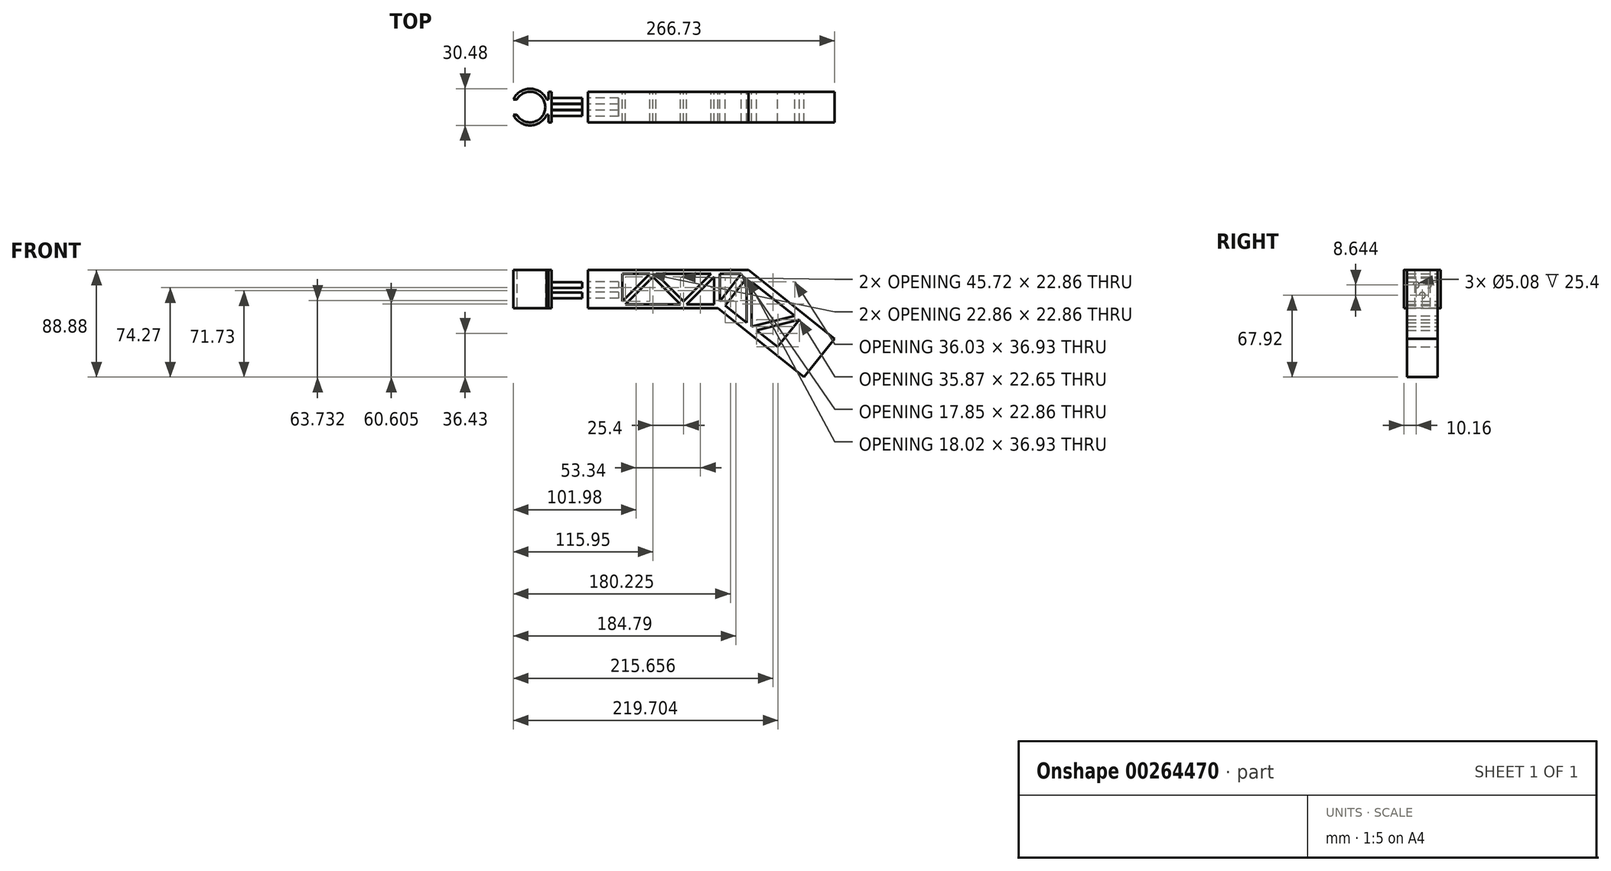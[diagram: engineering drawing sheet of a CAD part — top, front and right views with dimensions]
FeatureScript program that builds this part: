
annotation { "Feature Type Name" : "Feature", "Feature Type Description" : "" }
export const myFeature = defineFeature(function(context is Context, id is Id, definition is map)
    precondition{}
    {
        {
            var Q0;
            Q0=qCreatedBy(makeId("Front.planeOp"),FACE);
            var sketch = newSketch(context, id + "F0", { "sketchPlane" : qUnion([Q0])});
            skLineSegment(sketch, "E0.top", {"start": v(101.6, -25.4) * mm, "end": v(55.88, -25.4) * mm});
            skLineSegment(sketch, "E0.left", {"start": v(101.6, 20.32) * mm, "end": v(101.6, -25.4) * mm});
            skPoint(sketch, "E0.middle", {"position": v(0, 0) * mm});
            skLineSegment(sketch, "E1", {"start": v(-50.8, -20.32) * mm, "end": v(-5.08, 25.4) * mm});
            skLineSegment(sketch, "E2", {"start": v(-45.72, -25.4) * mm, "end": v(0, 20.32) * mm});
            skLineSegment(sketch, "E3", {"start": v(0, 20.32) * mm, "end": v(45.72, -25.4) * mm});
            skLineSegment(sketch, "E4", {"start": v(5.08, 25.4) * mm, "end": v(50.8, -20.32) * mm});
            skLineSegment(sketch, "E5", {"start": v(50.8, -20.32) * mm, "end": v(96.52, 25.4) * mm});
            skLineSegment(sketch, "E6", {"start": v(55.88, -25.4) * mm, "end": v(101.6, 20.32) * mm});
            skLineSegment(sketch, "E7.bottom", {"start": v(107.95, 31.75) * mm, "end": v(-107.95, 31.75) * mm});
            skLineSegment(sketch, "E7.top", {"start": v(107.95, -31.75) * mm, "end": v(-107.95, -31.75) * mm});
            skLineSegment(sketch, "E7.left", {"start": v(107.95, 31.75) * mm, "end": v(107.95, -31.75) * mm});
            skLineSegment(sketch, "E7.right", {"start": v(-107.95, 31.75) * mm, "end": v(-107.95, -31.75) * mm});
            skLineSegment(sketch, "E8", {"start": v(-50.8, 25.4) * mm, "end": v(-5.08, 25.4) * mm});
            skLineSegment(sketch, "E9", {"start": v(5.08, 25.4) * mm, "end": v(96.52, 25.4) * mm});
            skPoint(sketch, "E10.orphan", {"position": v(101.6, 25.4) * mm});
            skLineSegment(sketch, "E11.trimOffspring", {"start": v(45.72, -25.4) * mm, "end": v(-45.72, -25.4) * mm});
            skPoint(sketch, "E12.start.orphan", {"position": v(0, -25.4) * mm});
            skLineSegment(sketch, "E13", {"start": v(107.95, 31.75) * mm, "end": v(158.75, 31.75) * mm});
            skLineSegment(sketch, "E14", {"start": v(107.95, -31.75) * mm, "end": v(79.41, -67.42) * mm});
            skLineSegment(sketch, "E15", {"start": v(107.95, -31.75) * mm, "end": v(187.29, 67.42) * mm});
            skLineSegment(sketch, "E16", {"start": v(187.29, 67.42) * mm, "end": v(207.12, 51.55) * mm});
            skLineSegment(sketch, "E17", {"start": v(207.12, 51.55) * mm, "end": v(127.78, -47.62) * mm});
            skLineSegment(sketch, "E18", {"start": v(79.41, -67.42) * mm, "end": v(99.25, -83.29) * mm});
            skLineSegment(sketch, "E19", {"start": v(99.25, -83.29) * mm, "end": v(127.78, -47.62) * mm});
            skLineSegment(sketch, "E20", {"start": v(-50.8, -20.32) * mm, "end": v(-50.8, 25.4) * mm});
            skSolve(sketch);
        }
        {
            var Q0;
            {var subQ0=sQuery(id+"F0.wireOp",EDGE,"E7.left");Q0=makeQuery(id+"F0.imprint","IMPRINT",FACE,{"disambiguationData":[TD([[makeQuery(id+"F0.imprint","IMPRINT",EDGE,{"derivedFrom":subQ0}),1.0]])]});}
            var Q1;
            Q1=makeQuery(id+"F0.imprint","IMPRINT",FACE,{"disambiguationData":[TD([[makeQuery(id+"F0.imprint","IMPRINT",EDGE,{"derivedFrom":sQuery(id+"F0.wireOp",EDGE,"E0.top")}),1.0]])]});
            extrude(context, id + "F1", {"entities" : qUnion([Q0, Q1]), "depth" : 25.4 * mm});
        }
        {
            var Q0;
            {var subQ0=sQuery(id+"F0.wireOp",EDGE,"E7.left");Q0=makeQuery(id+"F0.imprint","IMPRINT",FACE,{"disambiguationData":[TD([[makeQuery(id+"F0.imprint","IMPRINT",EDGE,{"derivedFrom":subQ0}),1.0]])]});}
            var Q1;
            Q1=makeQuery(id+"F0.imprint","IMPRINT",FACE,{"disambiguationData":[TD([[makeQuery(id+"F0.imprint","IMPRINT",EDGE,{"derivedFrom":sQuery(id+"F0.wireOp",EDGE,"E0.top")}),1.0]])]});
            extrude(context, id + "F2", {"entities" : qUnion([Q0, Q1]), "operationType" : NewBodyOperationType.ADD, "oppositeDirection" : true, "depth" : 25.4 * mm});
        }
        {
            var Q0;
            Q0=makeQuery(id+"F1.opExtrude","SWEPT_BODY",BODY,{"disambiguationData":[OSD([sQuery(id+"F0.wireOp",EDGE,"E0.top"),sQuery(id+"F0.wireOp",EDGE,"E0.left"),sQuery(id+"F0.wireOp",EDGE,"E0.right"),sQuery(id+"F0.wireOp",EDGE,"QCtYprh2-Jfjn-PrE3-rnew-0jCrY2ncBvmK"),sQuery(id+"F0.wireOp",EDGE,"aiMvw6XH-L72F-sl51-ARJl-qKLrPWgA6oOl"),sQuery(id+"F0.wireOp",EDGE,"E1"),sQuery(id+"F0.wireOp",EDGE,"E2"),sQuery(id+"F0.wireOp",EDGE,"E3"),sQuery(id+"F0.wireOp",EDGE,"E4"),sQuery(id+"F0.wireOp",EDGE,"E5"),sQuery(id+"F0.wireOp",EDGE,"E6"),sQuery(id+"F0.wireOp",EDGE,"E7.bottom"),sQuery(id+"F0.wireOp",EDGE,"E7.top"),sQuery(id+"F0.wireOp",EDGE,"E7.right"),sQuery(id+"F0.wireOp",EDGE,"E8"),sQuery(id+"F0.wireOp",EDGE,"E9"),sQuery(id+"F0.wireOp",EDGE,"E11.trimOffspring"),sQuery(id+"F0.wireOp",EDGE,"40eba89f-6af4-46ac-b0d6-bf0ef43d7f53.trimOffspring"),sQuery(id+"F0.wireOp",EDGE,"E13"),sQuery(id+"F0.wireOp",EDGE,"E15")])]});
            var Q1;
            Q1=qCreatedBy(makeId("Origin.pointOp"),VERTEX);
            transform(context, id + "F3", {"entities" : qUnion([Q0]), "transformType" : TransformType.SCALE_UNIFORMLY, "scale" : .5, "scalePoint" : qUnion([Q1]), "makeCopy" : false});
        }
        {
            var Q0;
            {var subQ0=sQuery(id+"F0.wireOp",EDGE,"E13");var subQ1=sQuery(id+"F0.wireOp",EDGE,"E7.bottom");Q0=makeQuery(id+"F2.boolean.opBoolean","MERGE",FACE,{"derivedFrom":[makeQuery(id+"F1.opExtrude","SWEPT_FACE",FACE,{"disambiguationData":[OSD([subQ1,subQ0])]}),makeQuery(id+"F2.opExtrude","SWEPT_FACE",FACE,{"disambiguationData":[OSD([subQ1,subQ0])]})]});}
            var sketch = newSketch(context, id + "F4", { "sketchPlane" : qUnion([Q0])});
            skPoint(sketch, "E21.endSnap0", {"position": v(-53.98, 0) * mm});
            skArc(sketch, "E22", {"start": v(-88.04, -10.16) * mm, "mid": v(-71.68, -20.51) * mm, "end": v(-53.97, -12.7) * mm});
            skArc(sketch, "E23", {"start": v(-82.75, -10.16) * mm, "mid": v(-53.98, 0) * mm, "end": v(-82.75, 10.16) * mm});
            skPoint(sketch, "E21.start.orphan", {"position": v(-53.98, 0) * mm});
            skLineSegment(sketch, "E24", {"start": v(-88.04, -10.16) * mm, "end": v(-82.75, -10.16) * mm});
            skLineSegment(sketch, "E25.trimOffspring", {"start": v(-82.75, 10.16) * mm, "end": v(-88.04, 10.16) * mm});
            skLineSegment(sketch, "E26", {"start": v(-53.98, -12.7) * mm, "end": v(-53.98, 12.7) * mm});
            skArc(sketch, "E27.trimOffspring", {"start": v(-53.98, 12.7) * mm, "mid": v(-71.68, 20.51) * mm, "end": v(-88.04, 10.16) * mm});
            skSolve(sketch);
        }
        {
            var Q0;
            {var subQ0=sQuery(id+"F0.wireOp",EDGE,"E15");Q0=makeQuery(id+"F2.boolean.opBoolean","MERGE",FACE,{"derivedFrom":[makeQuery(id+"F1.opExtrude","SWEPT_FACE",FACE,{"disambiguationData":[OSD([subQ0])]}),makeQuery(id+"F2.opExtrude","SWEPT_FACE",FACE,{"disambiguationData":[OSD([subQ0])]})]});}
            extrude(context, id + "F5", {"entities" : qUnion([Q0]), "operationType" : NewBodyOperationType.ADD, "depth" : 66.04 * mm});
        }
        {
            var Q0;
            {var subQ0=sQuery(id+"F0.wireOp",EDGE,"E15");Q0=makeQuery(id+"F5.boolean.opBoolean","MERGE",FACE,{"derivedFrom":[makeQuery(id+"F2.opExtrude","CAP_FACE",FACE,{"disambiguationData":[OSD([sQuery(id+"F0.wireOp",EDGE,"E0.top"),sQuery(id+"F0.wireOp",EDGE,"E0.left"),sQuery(id+"F0.wireOp",EDGE,"E0.right"),sQuery(id+"F0.wireOp",EDGE,"QCtYprh2-Jfjn-PrE3-rnew-0jCrY2ncBvmK"),sQuery(id+"F0.wireOp",EDGE,"aiMvw6XH-L72F-sl51-ARJl-qKLrPWgA6oOl"),sQuery(id+"F0.wireOp",EDGE,"E1"),sQuery(id+"F0.wireOp",EDGE,"E2"),sQuery(id+"F0.wireOp",EDGE,"E3"),sQuery(id+"F0.wireOp",EDGE,"E4"),sQuery(id+"F0.wireOp",EDGE,"E5"),sQuery(id+"F0.wireOp",EDGE,"E6"),sQuery(id+"F0.wireOp",EDGE,"E7.bottom"),sQuery(id+"F0.wireOp",EDGE,"E7.top"),sQuery(id+"F0.wireOp",EDGE,"E7.right"),sQuery(id+"F0.wireOp",EDGE,"E8"),sQuery(id+"F0.wireOp",EDGE,"E9"),sQuery(id+"F0.wireOp",EDGE,"E11.trimOffspring"),sQuery(id+"F0.wireOp",EDGE,"40eba89f-6af4-46ac-b0d6-bf0ef43d7f53.trimOffspring"),sQuery(id+"F0.wireOp",EDGE,"E13"),subQ0])],"isStart":false}),makeQuery(id+"F5.opExtrude","SWEPT_FACE",FACE,{"disambiguationData":[OSD([subQ0]),TDD([makeQuery(id+"F2.opExtrude","CAP_EDGE",EDGE,{"disambiguationData":[OSD([subQ0])],"isStart":false})])]})]});}
            var sketch = newSketch(context, id + "F6", { "sketchPlane" : qUnion([Q0])});
            skLineSegment(sketch, "E28", {"start": v(-48.26, 12.7) * mm, "end": v(-55.35, 12.7) * mm});
            skLineSegment(sketch, "E29", {"start": v(-55.35, 12.7) * mm, "end": v(-55.35, -10.16) * mm});
            skLineSegment(sketch, "E30", {"start": v(-55.35, 12.7) * mm, "end": v(-73.2, 12.7) * mm});
            skLineSegment(sketch, "E31", {"start": v(-73.2, 12.7) * mm, "end": v(-55.35, -10.16) * mm});
            skLineSegment(sketch, "E32", {"start": v(-73.2, 12.7) * mm, "end": v(-77.69, 9.2) * mm});
            skLineSegment(sketch, "E33", {"start": v(-55.35, -10.16) * mm, "end": v(-59.83, -13.66) * mm});
            skLineSegment(sketch, "E34", {"start": v(-59.83, -13.66) * mm, "end": v(-77.69, 9.2) * mm});
            skLineSegment(sketch, "E35", {"start": v(-59.83, -13.66) * mm, "end": v(-77.85, -27.73) * mm});
            skLineSegment(sketch, "E36", {"start": v(-77.85, -27.73) * mm, "end": v(-77.69, 9.2) * mm});
            skLineSegment(sketch, "E37", {"start": v(-77.85, -27.73) * mm, "end": v(-81.85, -30.86) * mm});
            skLineSegment(sketch, "E38", {"start": v(-81.85, -30.86) * mm, "end": v(-99.7, -8) * mm});
            skLineSegment(sketch, "E39", {"start": v(-99.7, -8) * mm, "end": v(-81.7, 6.07) * mm});
            skLineSegment(sketch, "E40", {"start": v(-81.7, 6.07) * mm, "end": v(-81.85, -30.86) * mm});
            skLineSegment(sketch, "E41", {"start": v(-99.7, -8) * mm, "end": v(-117.72, -22.07) * mm});
            skLineSegment(sketch, "E42", {"start": v(-117.72, -22.07) * mm, "end": v(-81.85, -30.86) * mm});
            skLineSegment(sketch, "E43", {"start": v(-117.72, -22.07) * mm, "end": v(-121.69, -25.24) * mm});
            skLineSegment(sketch, "E44", {"start": v(-81.7, 6.07) * mm, "end": v(-77.69, 9.2) * mm});
            skLineSegment(sketch, "E45", {"start": v(-81.85, -30.86) * mm, "end": v(-85.82, -34.03) * mm});
            skLineSegment(sketch, "E46", {"start": v(-121.69, -25.24) * mm, "end": v(-85.82, -34.03) * mm});
            skLineSegment(sketch, "E47", {"start": v(-121.69, -25.24) * mm, "end": v(-103.57, -47.9) * mm});
            skLineSegment(sketch, "E48", {"start": v(-103.57, -47.9) * mm, "end": v(-85.82, -34.03) * mm});
            skSolve(sketch);
        }
        {
            var Q0;
            Q0=makeQuery(id+"F5.opExtrude","CAP_FACE",FACE,{"disambiguationData":[OSD([sQuery(id+"F0.wireOp",EDGE,"E15")])],"isStart":false});
            var sketch = newSketch(context, id + "F7", { "sketchPlane" : qUnion([Q0])});
            skPoint(sketch, "E49.middle", {"position": v(-1.87, 41.42) * mm});
            skLineSegment(sketch, "E50.bottom", {"start": v(48.93, 92.22) * mm, "end": v(-52.67, 92.22) * mm});
            skLineSegment(sketch, "E50.top", {"start": v(48.93, -9.38) * mm, "end": v(-52.67, -9.38) * mm});
            skLineSegment(sketch, "E50.left", {"start": v(48.93, 92.22) * mm, "end": v(48.93, -9.38) * mm});
            skLineSegment(sketch, "E50.right", {"start": v(-52.67, 92.22) * mm, "end": v(-52.67, -9.38) * mm});
            skSolve(sketch);
        }
        {
            var Q0;
            Q0=makeQuery(id+"F7.imprint","IMPRINT",FACE,{"disambiguationData":[TD([[makeQuery(id+"F7.imprint","IMPRINT",EDGE,{"derivedFrom":sQuery(id+"F7.wireOp",EDGE,"E49.bottom")}),1.0]])]});
            var Q1;
            {var subQ1=sQuery(id+"F0.wireOp",EDGE,"E15");var subQ2=makeQuery(id+"F5.opExtrude","CAP_EDGE",EDGE,{"disambiguationData":[OSD([subQ1]),TDD([makeQuery(id+"F1.opExtrude","CAP_EDGE",EDGE,{"disambiguationData":[OSD([subQ1])],"isStart":false})])],"isStart":false});Q1=makeQuery(id+"F7.imprint","IMPRINT",FACE,{"disambiguationData":[TD([[makeQuery(id+"F7.imprint","IMPRINT",EDGE,{"derivedFrom":subQ2}),-1.0]])]});}
            var Q2;
            {var subQ1=sQuery(id+"F0.wireOp",EDGE,"E15");var subQ2=makeQuery(id+"F5.opExtrude","CAP_EDGE",EDGE,{"disambiguationData":[OSD([sQuery(id+"F0.wireOp",EDGE,"E7.top"),sQuery(id+"F0.wireOp",EDGE,"E7.left"),sQuery(id+"F0.wireOp",EDGE,"E14"),subQ1])],"isStart":false});Q2=makeQuery(id+"F7.imprint","IMPRINT",FACE,{"disambiguationData":[TD([[makeQuery(id+"F7.imprint","IMPRINT",EDGE,{"derivedFrom":subQ2}),1.0]])]});}
            var Q3;
            {var subQ1=sQuery(id+"F0.wireOp",EDGE,"E15");var subQ2=makeQuery(id+"F5.opExtrude","CAP_EDGE",EDGE,{"disambiguationData":[OSD([subQ1]),TDD([makeQuery(id+"F2.opExtrude","CAP_EDGE",EDGE,{"disambiguationData":[OSD([subQ1])],"isStart":false})])],"isStart":false});Q3=makeQuery(id+"F7.imprint","IMPRINT",FACE,{"disambiguationData":[TD([[makeQuery(id+"F7.imprint","IMPRINT",EDGE,{"derivedFrom":subQ2}),1.0]])]});}
            var Q4;
            {var subQ1=sQuery(id+"F0.wireOp",EDGE,"E15");var subQ2=makeQuery(id+"F5.opExtrude","CAP_EDGE",EDGE,{"disambiguationData":[OSD([sQuery(id+"F0.wireOp",EDGE,"E13"),subQ1])],"isStart":false});Q4=makeQuery(id+"F7.imprint","IMPRINT",FACE,{"disambiguationData":[TD([[makeQuery(id+"F7.imprint","IMPRINT",EDGE,{"derivedFrom":subQ2}),-1.0]])]});}
            extrude(context, id + "F8", {"entities" : qUnion([Q0, Q1, Q2, Q3, Q4]), "operationType" : NewBodyOperationType.ADD, "depth" : 25.4 * mm});
        }
        {
            var Q0;
            Q0=makeQuery(id+"F6.imprint","IMPRINT",FACE,{"disambiguationData":[TD([[makeQuery(id+"F6.imprint","IMPRINT",EDGE,{"derivedFrom":sQuery(id+"F6.wireOp",EDGE,"E46")}),-1.0]])]});
            var Q1;
            Q1=makeQuery(id+"F6.imprint","IMPRINT",FACE,{"disambiguationData":[TD([[makeQuery(id+"F6.imprint","IMPRINT",EDGE,{"derivedFrom":sQuery(id+"F6.wireOp",EDGE,"E38")}),1.0]])]});
            var Q2;
            Q2=makeQuery(id+"F6.imprint","IMPRINT",FACE,{"disambiguationData":[TD([[makeQuery(id+"F6.imprint","IMPRINT",EDGE,{"derivedFrom":sQuery(id+"F6.wireOp",EDGE,"E38")}),-1.0]])]});
            var Q3;
            Q3=makeQuery(id+"F6.imprint","IMPRINT",FACE,{"disambiguationData":[TD([[makeQuery(id+"F6.imprint","IMPRINT",EDGE,{"derivedFrom":sQuery(id+"F6.wireOp",EDGE,"E34")}),1.0]])]});
            var Q4;
            Q4=makeQuery(id+"F6.imprint","IMPRINT",FACE,{"disambiguationData":[TD([[makeQuery(id+"F6.imprint","IMPRINT",EDGE,{"derivedFrom":sQuery(id+"F6.wireOp",EDGE,"E29")}),-1.0]])]});
            extrude(context, id + "F9", {"entities" : qUnion([Q0, Q1, Q2, Q3, Q4]), "operationType" : NewBodyOperationType.REMOVE, "oppositeDirection" : true, "depth" : 25.4 * mm});
        }
        {
            var Q0;
            {var subQ5=sQuery(id+"F4.wireOp",EDGE,"E25.trimOffspring");Q0=makeQuery(id+"F4.imprint","IMPRINT",FACE,{"disambiguationData":[TD([[makeQuery(id+"F4.imprint","IMPRINT",EDGE,{"derivedFrom":subQ5}),-1.0]])]});}
            var Q1;
            {var subQ5=sQuery(id+"F4.wireOp",EDGE,"E24");Q1=makeQuery(id+"F4.imprint","IMPRINT",FACE,{"disambiguationData":[TD([[makeQuery(id+"F4.imprint","IMPRINT",EDGE,{"derivedFrom":subQ5}),-1.0]])]});}
            extrude(context, id + "F10", {"entities" : qUnion([Q0, Q1]), "operationType" : NewBodyOperationType.REMOVE, "oppositeDirection" : true, "depth" : 31.75 * mm});
        }
        {
            var Q0;
            {var subQ0=sQuery(id+"F4.wireOp",EDGE,"E25.trimOffspring");Q0=makeQuery(id+"F4.imprint","IMPRINT",FACE,{"disambiguationData":[TD([[makeQuery(id+"F4.imprint","IMPRINT",EDGE,{"derivedFrom":subQ0}),-1.0]])]});}
            var Q1;
            {var subQ0=sQuery(id+"F4.wireOp",EDGE,"E22");Q1=makeQuery(id+"F4.imprint","IMPRINT",FACE,{"disambiguationData":[TD([[makeQuery(id+"F4.imprint","IMPRINT",EDGE,{"derivedFrom":subQ0}),1.0]])]});}
            extrude(context, id + "F11", {"entities" : qUnion([Q0, Q1]), "operationType" : NewBodyOperationType.REMOVE, "oppositeDirection" : true, "depth" : 25.4 * mm});
        }
        {
            var Q0;
            {var subQ0=sQuery(id+"F0.wireOp",EDGE,"E7.right");Q0=makeQuery(id+"F2.boolean.opBoolean","MERGE",FACE,{"derivedFrom":[makeQuery(id+"F1.opExtrude","SWEPT_FACE",FACE,{"disambiguationData":[OSD([subQ0])]}),makeQuery(id+"F2.opExtrude","SWEPT_FACE",FACE,{"disambiguationData":[OSD([subQ0])]})]});}
            var sketch = newSketch(context, id + "F12", { "sketchPlane" : qUnion([Q0])});
            skCircle(sketch, "E51", {"center": v(-5.08, 3.53) * mm, "radius": 2.54 * mm});
            skCircle(sketch, "E52", {"center": v(5.08, 3.56) * mm, "radius": 2.54 * mm});
            skCircle(sketch, "E53", {"center": v(0, -5.08) * mm, "radius": 2.54 * mm});
            skSolve(sketch);
        }
        {
            var Q0;
            Q0 = qSketchRegion(id + "F12", true);
            extrude(context, id + "F13", {"entities" : qUnion([Q0]), "operationType" : NewBodyOperationType.REMOVE, "oppositeDirection" : true, "depth" : 25.4 * mm});
        }
        {
            var Q0;
            Q0=qCreatedBy(makeId("Top.planeOp"),FACE);
            var sketch = newSketch(context, id + "F14", { "sketchPlane" : qUnion([Q0])});
            skArc(sketch, "E54", {"start": v(-113.1, -6.35) * mm, "mid": v(-89.4, 0) * mm, "end": v(-113.1, 6.35) * mm});
            skArc(sketch, "E55", {"start": v(-115.95, -6.35) * mm, "mid": v(-102.1, -15.24) * mm, "end": v(-88.24, -6.35) * mm});
            skLineSegment(sketch, "E56", {"start": v(-113.1, 6.35) * mm, "end": v(-115.95, 6.35) * mm});
            skLineSegment(sketch, "E57", {"start": v(-113.1, -6.35) * mm, "end": v(-115.95, -6.35) * mm});
            skLineSegment(sketch, "E58", {"start": v(-86.85, 6.35) * mm, "end": v(-86.85, 12.7) * mm});
            skLineSegment(sketch, "E59", {"start": v(-86.85, -6.35) * mm, "end": v(-86.85, -12.7) * mm});
            skLineSegment(sketch, "E60", {"start": v(-86.85, 12.7) * mm, "end": v(-84.31, 12.7) * mm});
            skLineSegment(sketch, "E61", {"start": v(-84.31, 12.7) * mm, "end": v(-84.31, -12.7) * mm});
            skLineSegment(sketch, "E62", {"start": v(-84.31, -12.7) * mm, "end": v(-86.85, -12.7) * mm});
            skLineSegment(sketch, "E63", {"start": v(-86.85, -6.35) * mm, "end": v(-88.24, -6.35) * mm});
            skLineSegment(sketch, "E64", {"start": v(-86.85, 6.35) * mm, "end": v(-88.24, 6.35) * mm});
            skPoint(sketch, "E65.orphan", {"position": v(-86.85, 0) * mm});
            skArc(sketch, "E66.trimOffspring", {"start": v(-88.24, 6.35) * mm, "mid": v(-102.1, 15.24) * mm, "end": v(-115.95, 6.35) * mm});
            skSolve(sketch);
        }
        {
            var Q0;
            Q0=makeQuery(id+"F14.imprint","IMPRINT",FACE,{"disambiguationData":[TD([[makeQuery(id+"F14.imprint","IMPRINT",EDGE,{"derivedFrom":sQuery(id+"F14.wireOp",EDGE,"E54")}),-1.0]])]});
            var Q1;
            Q1=makeQuery(id+"F14.imprint","IMPRINT",FACE,{"disambiguationData":[TD([[makeQuery(id+"F14.imprint","IMPRINT",EDGE,{"derivedFrom":sQuery(id+"F14.wireOp",EDGE,"E58")}),-1.0]])]});
            extrude(context, id + "F15", {"entities" : qUnion([Q0, Q1]), "depth" : 15.88 * mm, "hasSecondDirection" : true, "secondDirectionOppositeDirection" : true, "secondDirectionDepth" : 15.88 * mm});
        }
        {
            var Q0;
            Q0=makeQuery(id+"F15.opExtrude","SWEPT_FACE",FACE,{"disambiguationData":[OSD([sQuery(id+"F14.wireOp",EDGE,"E61")])]});
            var sketch = newSketch(context, id + "F16", { "sketchPlane" : qUnion([Q0])});
            skLineSegment(sketch, "E67", {"start": v(0, 15.88) * mm, "end": v(0, -15.88) * mm});
            skLineSegment(sketch, "E68", {"start": v(-12.7, 0) * mm, "end": v(12.7, 0) * mm});
            skLineSegment(sketch, "E69", {"start": v(0, 0) * mm, "end": v(-5.1, 0) * mm});
            skLineSegment(sketch, "E70", {"start": v(-5.1, 0) * mm, "end": v(-5.1, 3.53) * mm});
            skCircle(sketch, "E71", {"center": v(-5.1, 3.53) * mm, "radius": 2.41 * mm});
            skLineSegment(sketch, "E72", {"start": v(0, 0) * mm, "end": v(5.08, 0) * mm});
            skLineSegment(sketch, "E73", {"start": v(5.08, 0) * mm, "end": v(5.08, 3.53) * mm});
            skCircle(sketch, "E74", {"center": v(5.08, 3.53) * mm, "radius": 2.41 * mm});
            skLineSegment(sketch, "E75", {"start": v(0, 0) * mm, "end": v(0, -5.08) * mm});
            skCircle(sketch, "E76", {"center": v(0, -5.08) * mm, "radius": 2.41 * mm});
            skSolve(sketch);
        }
        {
            var Q0;
            Q0 = qSketchRegion(id + "F16", true);
            extrude(context, id + "F17", {"entities" : qUnion([Q0]), "operationType" : NewBodyOperationType.ADD, "depth" : 25.4 * mm});
        }
    });
